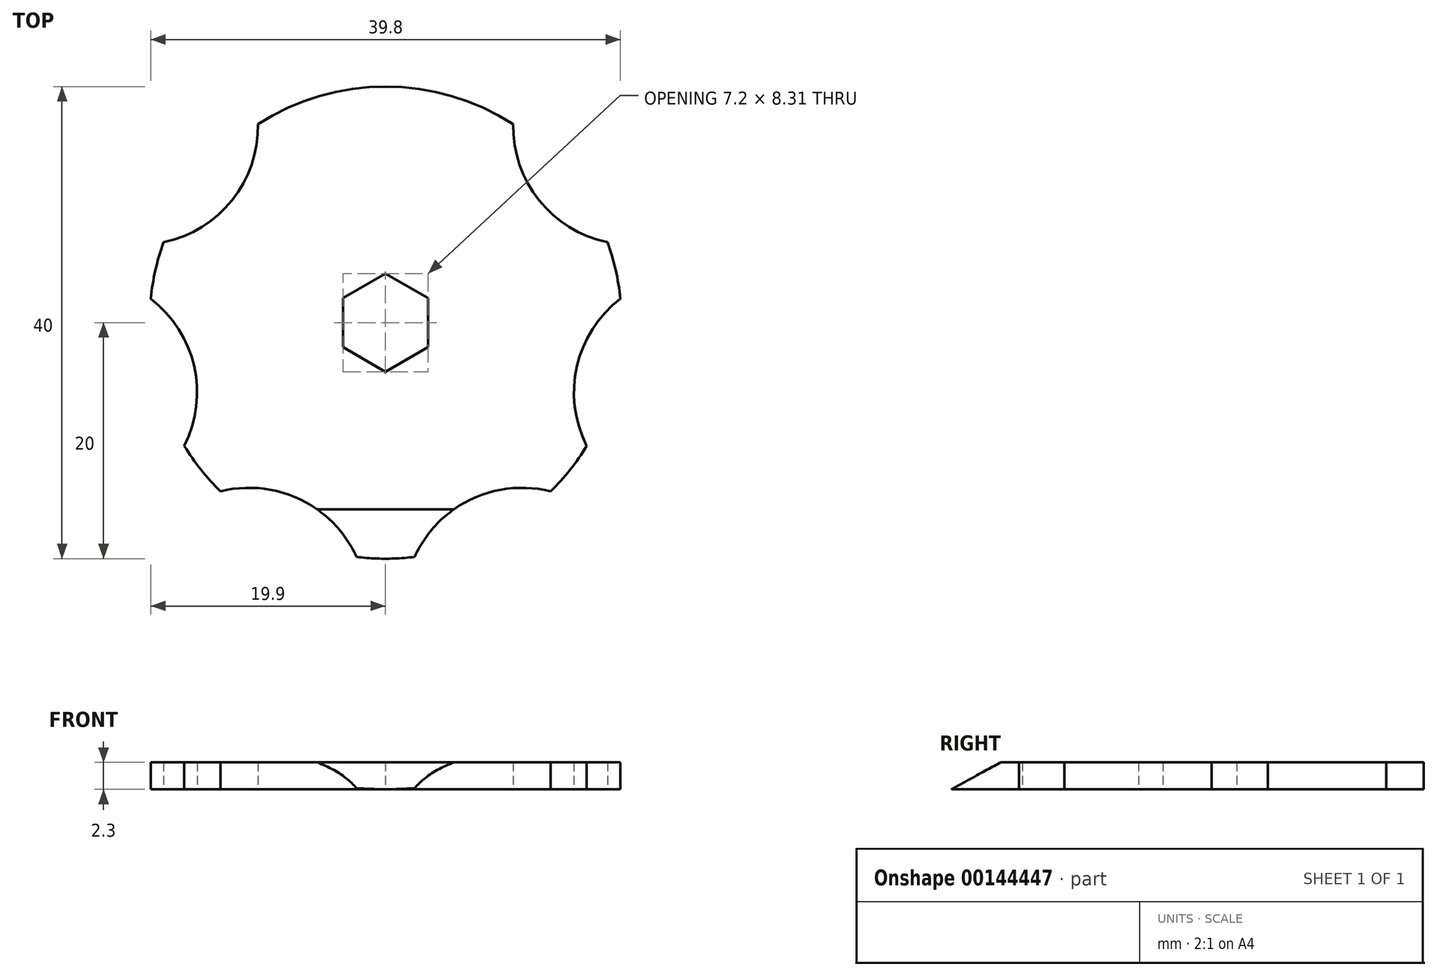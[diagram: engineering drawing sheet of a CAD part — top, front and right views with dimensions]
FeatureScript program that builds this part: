
annotation { "Feature Type Name" : "Feature", "Feature Type Description" : "" }
export const myFeature = defineFeature(function(context is Context, id is Id, definition is map)
    precondition{}
    {
        {
            var Q0;
            Q0=qCreatedBy(makeId("Top.planeOp"),FACE);
            var sketch = newSketch(context, id + "F0", { "sketchPlane" : qUnion([Q0])});
            skCircle(sketch, "E0.cCircle", {"center": v(0, 0) * mm, "radius": 3.6 * mm, "construction": true});
            skLineSegment(sketch, "E0.0", {"start": v(3.6, 2.08) * mm, "end": v(3.6, -2.08) * mm});
            skLineSegment(sketch, "E0.1", {"start": v(3.6, -2.08) * mm, "end": v(0, -4.16) * mm});
            skLineSegment(sketch, "E0.2", {"start": v(0, -4.16) * mm, "end": v(-3.6, -2.08) * mm});
            skLineSegment(sketch, "E0.3", {"start": v(-3.6, -2.08) * mm, "end": v(-3.6, 2.08) * mm});
            skLineSegment(sketch, "E0.4", {"start": v(-3.6, 2.08) * mm, "end": v(0, 4.16) * mm});
            skLineSegment(sketch, "E0.5", {"start": v(0, 4.16) * mm, "end": v(3.6, 2.08) * mm});
            skPoint(sketch, "E0.0.midPoint", {"position": v(3.6, 0) * mm});
            skCircle(sketch, "E1", {"center": v(0, 0) * mm, "radius": 20 * mm});
            skSolve(sketch);
        }
        {
            var Q0;
            Q0=makeQuery(id+"F0.imprint","IMPRINT",FACE,{"disambiguationData":[TD([[makeQuery(id+"F0.imprint","IMPRINT",EDGE,{"derivedFrom":sQuery(id+"F0.wireOp",EDGE,"E0.0")}),1.0]])]});
            extrude(context, id + "F1", {"entities" : qUnion([Q0]), "depth" : 2.3 * mm});
        }
        {
            var Q0;
            Q0=qCreatedBy(makeId("Top.planeOp"),FACE);
            var sketch = newSketch(context, id + "F2", { "sketchPlane" : qUnion([Q0])});
            skCircle(sketch, "E2.1.0", {"center": v(-20.82, 16.6) * mm, "radius": 10 * mm});
            skCircle(sketch, "E2.2.0", {"center": v(-25.97, -5.93) * mm, "radius": 10 * mm});
            skCircle(sketch, "E2.3.0", {"center": v(-11.56, -24) * mm, "radius": 10 * mm});
            skCircle(sketch, "E2.4.0", {"center": v(11.56, -24) * mm, "radius": 10 * mm});
            skCircle(sketch, "E2.5.0", {"center": v(25.97, -5.93) * mm, "radius": 10 * mm});
            skCircle(sketch, "E2.6.0", {"center": v(20.82, 16.6) * mm, "radius": 10 * mm});
            skPoint(sketch, "E2.center", {"position": v(0, 0) * mm});
            skSolve(sketch);
        }
        {
            var Q0;
            Q0=qSketchRegion(id+"F2",true);
            extrude(context, id + "F3", {"entities" : qUnion([Q0]), "operationType" : NewBodyOperationType.REMOVE, "endBound" : BoundingType.THROUGH_ALL, "depth" : 25 * mm});
        }
        {
            var Q0;
            Q0=qCreatedBy(makeId("Right.planeOp"),FACE);
            var sketch = newSketch(context, id + "F4", { "sketchPlane" : qUnion([Q0])});
            skLineSegment(sketch, "E3", {"start": v(-20.03, 0) * mm, "end": v(-20.03, 3) * mm});
            skLineSegment(sketch, "E4", {"start": v(-20.03, 3) * mm, "end": v(-14.53, 3) * mm});
            skLineSegment(sketch, "E5", {"start": v(-14.53, 3) * mm, "end": v(-20.03, 0) * mm});
            skSolve(sketch);
        }
        {
            var Q0;
            Q0 = qSketchRegion(id + "F4", true);
            extrude(context, id + "F5", {"entities" : qUnion([Q0]), "operationType" : NewBodyOperationType.REMOVE, "endBound" : BoundingType.SYMMETRIC, "oppositeDirection" : true, "depth" : 12 * mm});
        }
        {
            var Q0;
            {var subQ0=sQuery(id+"F0.wireOp",EDGE,"E1");Q0=makeQuery(id+"F3.boolean.opBoolean","SPLIT",EDGE,{"disambiguationData":[TD([makeQuery(id+"F1.opExtrude","CAP_FACE",FACE,{"disambiguationData":[OSD([sQuery(id+"F0.wireOp",EDGE,"E0.0"),sQuery(id+"F0.wireOp",EDGE,"E0.1"),sQuery(id+"F0.wireOp",EDGE,"E0.2"),sQuery(id+"F0.wireOp",EDGE,"E0.3"),sQuery(id+"F0.wireOp",EDGE,"E0.4"),sQuery(id+"F0.wireOp",EDGE,"E0.5"),subQ0])],"isStart":false}),makeQuery(id+"F1.opExtrude","SWEPT_FACE",FACE,{"disambiguationData":[OSD([subQ0])]}),makeQuery(id+"F3.opExtrude","SWEPT_FACE",FACE,{"disambiguationData":[OSD([sQuery(id+"F2.wireOp",EDGE,"E2.2.0")])]}),makeQuery(id+"F3.opExtrude","SWEPT_FACE",FACE,{"disambiguationData":[OSD([sQuery(id+"F2.wireOp",EDGE,"E2.3.0")])]})])],"derivedFrom":makeQuery(id+"F1.opExtrude","CAP_EDGE",EDGE,{"disambiguationData":[OSD([subQ0])],"isStart":false})});}
            cPoint(context, id + "F6", {"entities" : qUnion([Q0]), "parameter" : 0.5});
        }
        {
            var Q0;
            {var subQ0=sQuery(id+"F0.wireOp",EDGE,"E1");Q0=makeQuery(id+"F3.boolean.opBoolean","SPLIT",EDGE,{"disambiguationData":[TD([makeQuery(id+"F1.opExtrude","CAP_FACE",FACE,{"disambiguationData":[OSD([sQuery(id+"F0.wireOp",EDGE,"E0.0"),sQuery(id+"F0.wireOp",EDGE,"E0.1"),sQuery(id+"F0.wireOp",EDGE,"E0.2"),sQuery(id+"F0.wireOp",EDGE,"E0.3"),sQuery(id+"F0.wireOp",EDGE,"E0.4"),sQuery(id+"F0.wireOp",EDGE,"E0.5"),subQ0])],"isStart":true}),makeQuery(id+"F1.opExtrude","SWEPT_FACE",FACE,{"disambiguationData":[OSD([subQ0])]}),makeQuery(id+"F3.opExtrude","SWEPT_FACE",FACE,{"disambiguationData":[OSD([sQuery(id+"F2.wireOp",EDGE,"E2.2.0")])]}),makeQuery(id+"F3.opExtrude","SWEPT_FACE",FACE,{"disambiguationData":[OSD([sQuery(id+"F2.wireOp",EDGE,"E2.3.0")])]})])],"derivedFrom":makeQuery(id+"F1.opExtrude","CAP_EDGE",EDGE,{"disambiguationData":[OSD([subQ0])],"isStart":true})});}
            cPoint(context, id + "F7", {"entities" : qUnion([Q0]), "parameter" : 0.5});
        }
        {
            var Q0;
            Q0 = qCreatedBy(id + "F6" ,VERTEX);
            var Q1;
            Q1 = qCreatedBy(id + "F7" ,VERTEX);
            var Q2;
            Q2=qCreatedBy(makeId("Origin.pointOp"),VERTEX);
            cPlane(context, id + "F8", {"entities" : qUnion([Q0, Q1, Q2]), "cplaneType" : CPlaneType.THREE_POINT, "offset" : 25 * mm, "width" : 150 * mm, "height" : 150 * mm});
        }
    });
